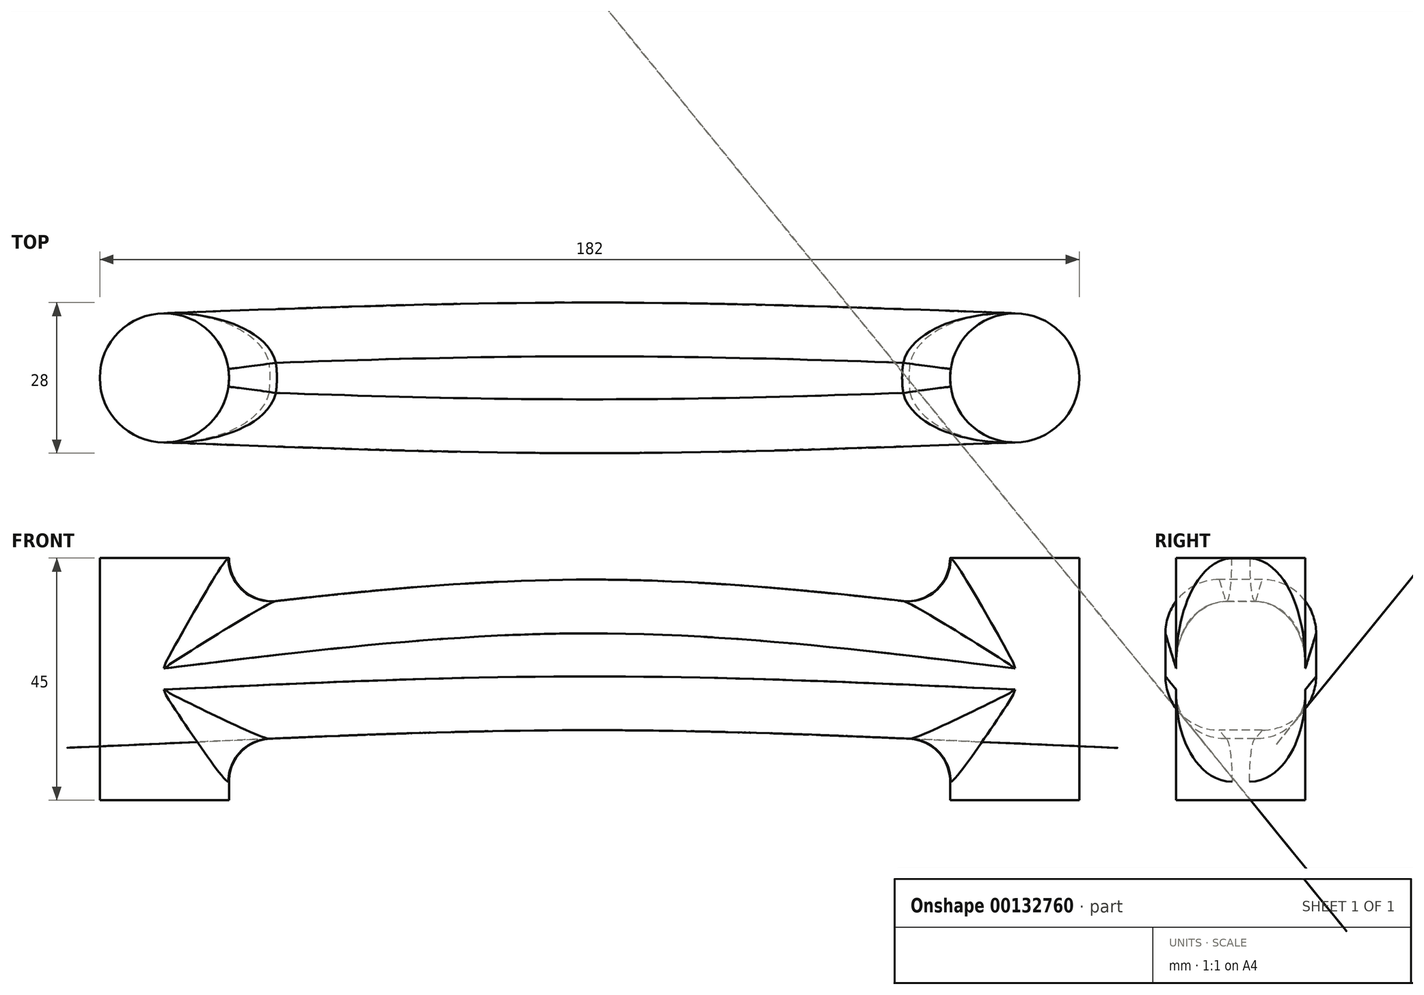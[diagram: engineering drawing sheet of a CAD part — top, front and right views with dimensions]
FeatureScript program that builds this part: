
annotation { "Feature Type Name" : "Feature", "Feature Type Description" : "" }
export const myFeature = defineFeature(function(context is Context, id is Id, definition is map)
    precondition{}
    {
        {
            var Q0;
            Q0=qCreatedBy(makeId("Top.planeOp"),FACE);
            var sketch = newSketch(context, id + "F0", { "sketchPlane" : qUnion([Q0])});
            skCircle(sketch, "E0", {"center": v(79, 0) * mm, "radius": 12 * mm});
            skLineSegment(sketch, "E1", {"start": v(-79, 0) * mm, "end": v(79, 0) * mm, "construction": true});
            skSolve(sketch);
        }
        {
            var Q0;
            Q0=makeQuery(id+"F0.imprint","IMPRINT",FACE,{"disambiguationData":[TD([[makeQuery(id+"F0.imprint","IMPRINT",EDGE,{"derivedFrom":sQuery(id+"F0.wireOp",EDGE,"rZ54wsOb-oDF6-y7NS-FH1f-pCdBLFLm0OSo")}),1.0]])]});
            var Q1;
            Q1=makeQuery(id+"F0.imprint","IMPRINT",FACE,{"disambiguationData":[TD([[makeQuery(id+"F0.imprint","IMPRINT",EDGE,{"derivedFrom":sQuery(id+"F0.wireOp",EDGE,"E0")}),1.0]])]});
            extrude(context, id + "F1", {"entities" : qUnion([Q0, Q1]), "depth" : 45 * mm});
        }
        {
            var Q0;
            Q0=qCreatedBy(makeId("Right.planeOp"),FACE);
            cPlane(context, id + "F2", {"entities" : qUnion([Q0]), "cplaneType" : CPlaneType.OFFSET, "offset" : (158 / 2) * mm, "width" : 150 * mm, "height" : 150 * mm});
        }
        {
            var Q0;
            Q0=qCreatedBy(id+"F2.planeOp",FACE);
            var sketch = newSketch(context, id + "F3", { "sketchPlane" : qUnion([Q0])});
            skLineSegment(sketch, "E2.bottom", {"start": v(-12, 34.5) * mm, "end": v(12, 34.5) * mm});
            skLineSegment(sketch, "E2.top", {"start": v(-12, 10.5) * mm, "end": v(12, 10.5) * mm});
            skLineSegment(sketch, "E2.left", {"start": v(-12, 34.5) * mm, "end": v(-12, 10.5) * mm});
            skLineSegment(sketch, "E2.right", {"start": v(12, 34.5) * mm, "end": v(12, 10.5) * mm});
            skLineSegment(sketch, "E3", {"start": v(0, 0) * mm, "end": v(0, 10.5) * mm});
            skSolve(sketch);
        }
        {
            var Q0;
            Q0=qCreatedBy(makeId("Right.planeOp"),FACE);
            var sketch = newSketch(context, id + "F4", { "sketchPlane" : qUnion([Q0])});
            skLineSegment(sketch, "E4.bottom", {"start": v(14, 41) * mm, "end": v(-14, 41) * mm});
            skLineSegment(sketch, "E4.top", {"start": v(14, 13) * mm, "end": v(-14, 13) * mm});
            skLineSegment(sketch, "E4.left", {"start": v(14, 41) * mm, "end": v(14, 13) * mm});
            skLineSegment(sketch, "E4.right", {"start": v(-14, 41) * mm, "end": v(-14, 13) * mm});
            skLineSegment(sketch, "E5", {"start": v(0, 0) * mm, "end": v(0, 13) * mm});
            skSolve(sketch);
        }
        {
            var Q1;
            Q1=makeQuery(id+"F4.imprint","IMPRINT",FACE,{"disambiguationData":[TD([[makeQuery(id+"F4.imprint","IMPRINT",EDGE,{"derivedFrom":sQuery(id+"F4.wireOp",EDGE,"E4.bottom")}),1.0]])]});
            var Q2;
            Q2=makeQuery(id+"F3.imprint","IMPRINT",FACE,{"disambiguationData":[TD([[makeQuery(id+"F3.imprint","IMPRINT",EDGE,{"derivedFrom":sQuery(id+"F3.wireOp",EDGE,"E2.bottom")}),-1.0]])]});
            loft(context, id + "F5", {"operationType" : NewBodyOperationType.ADD, "startCondition" : LoftEndDerivativeType.NORMAL_TO_PROFILE, "startMagnitude" : 1, "sheetProfilesArray" : [{ "sheetProfileEntities" : qUnion([Q1]) }, { "sheetProfileEntities" : qUnion([Q2]) }]});
        }
        {
            var Q0;
            Q0=makeQuery(id+"F5.opLoft","SWEPT_EDGE",EDGE,{"disambiguationData":[OSD([sQuery(id+"F3.wireOp",EDGE,"E2.top"),sQuery(id+"F3.wireOp",EDGE,"E2.left"),sQuery(id+"F4.wireOp",EDGE,"E4.top"),sQuery(id+"F4.wireOp",EDGE,"E4.right")])]});
            var Q1;
            Q1=makeQuery(id+"F5.opLoft","SWEPT_EDGE",EDGE,{"disambiguationData":[OSD([sQuery(id+"F3.wireOp",EDGE,"E2.bottom"),sQuery(id+"F3.wireOp",EDGE,"E2.left"),sQuery(id+"F4.wireOp",EDGE,"E4.bottom"),sQuery(id+"F4.wireOp",EDGE,"E4.right")])]});
            var Q2;
            Q2=makeQuery(id+"F5.opLoft","SWEPT_EDGE",EDGE,{"disambiguationData":[OSD([sQuery(id+"F3.wireOp",EDGE,"E2.top"),sQuery(id+"F3.wireOp",EDGE,"E2.right"),sQuery(id+"F4.wireOp",EDGE,"E4.top"),sQuery(id+"F4.wireOp",EDGE,"E4.left")])]});
            var Q3;
            Q3=makeQuery(id+"F5.opLoft","SWEPT_EDGE",EDGE,{"disambiguationData":[OSD([sQuery(id+"F3.wireOp",EDGE,"E2.bottom"),sQuery(id+"F3.wireOp",EDGE,"E2.right"),sQuery(id+"F4.wireOp",EDGE,"E4.bottom"),sQuery(id+"F4.wireOp",EDGE,"E4.left")])]});
            fillet(context, id + "F6", {"entities" : qUnion([Q0, Q1, Q2, Q3]), "radius" : 10 * mm, "tangentPropagation" : true, "allowEdgeOverflow" : false});
        }
        {
            var Q0;
            Q0=makeQuery(id+"F6.opFillet","BLEND_EDGE",EDGE,{"blendedFrom":[makeQuery(id+"F5.opLoft","SWEPT_EDGE",EDGE,{"disambiguationData":[OSD([sQuery(id+"F3.wireOp",EDGE,"E2.bottom"),sQuery(id+"F3.wireOp",EDGE,"E2.left"),sQuery(id+"F4.wireOp",EDGE,"E4.bottom"),sQuery(id+"F4.wireOp",EDGE,"E4.right")])]}),makeQuery(id+"F1.opExtrude","SWEPT_FACE",FACE,{"disambiguationData":[OSD([sQuery(id+"F0.wireOp",EDGE,"E0")])]})],"blendedInto":[makeQuery(id+"F1.opExtrude","SWEPT_FACE",FACE,{"disambiguationData":[OSD([sQuery(id+"F0.wireOp",EDGE,"E0")])]})]});
            var Q1;
            Q1=makeQuery(id+"F6.opFillet","BLEND_EDGE",EDGE,{"blendedFrom":[makeQuery(id+"F5.opLoft","SWEPT_EDGE",EDGE,{"disambiguationData":[OSD([sQuery(id+"F3.wireOp",EDGE,"E2.top"),sQuery(id+"F3.wireOp",EDGE,"E2.left"),sQuery(id+"F4.wireOp",EDGE,"E4.top"),sQuery(id+"F4.wireOp",EDGE,"E4.right")])]}),makeQuery(id+"F1.opExtrude","SWEPT_FACE",FACE,{"disambiguationData":[OSD([sQuery(id+"F0.wireOp",EDGE,"E0")])]})],"blendedInto":[makeQuery(id+"F1.opExtrude","SWEPT_FACE",FACE,{"disambiguationData":[OSD([sQuery(id+"F0.wireOp",EDGE,"E0")])]})]});
            fillet(context, id + "F7", {"entities" : qUnion([Q0, Q1]), "radius" : 8 * mm, "tangentPropagation" : true, "allowEdgeOverflow" : false});
        }
        {
            var Q0;
            Q0=makeQuery(id+"F1.opExtrude","SWEPT_BODY",BODY,{"disambiguationData":[OSD([sQuery(id+"F0.wireOp",EDGE,"E0")])]});
            var Q1;
            Q1=makeQuery(id+"F5.opLoft","CAP_FACE",FACE,{"disambiguationData":[OSD([makeQuery(id+"F4.imprint","IMPRINT",FACE,{"disambiguationData":[TD([[makeQuery(id+"F4.imprint","IMPRINT",EDGE,{"derivedFrom":sQuery(id+"F4.wireOp",EDGE,"E4.bottom")}),1.0]])]})])],"isStart":true});
            mirror(context, id + "F8", {"operationType" : NewBodyOperationType.ADD, "entities" : qUnion([Q0]), "mirrorPlane" : qUnion([Q1])});
        }
    });
